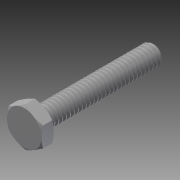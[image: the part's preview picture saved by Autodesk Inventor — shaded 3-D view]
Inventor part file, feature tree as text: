
AUTODESK INVENTOR PART (.ipt)
format: ipt  version: 2014 SP1 (Build 180222100, 222)  size: 806,912 bytes
history: native  units: in
note: dims shown in document units (in); Inventor stores cm internally (conversion verified against a paired STEP export)
features: extrude x1, other x1, imported_body x1
ambient origin geometry x8: Origin, YZ Plane, XZ Plane, XY Plane, X Axis, Y Axis, Z Axis, Center Point
bodies: Body1 (feature_tree)
feature tree (3):
  extrude  "Extrude14"  [1 undecoded]
  other  "92620A5461"
  imported_body  "Base1"
note: 1 required parameter value undecoded (feature->parameter linkage not recoverable at this tier; creation-order binding heuristic only, values carry confidence <= 0.55)
